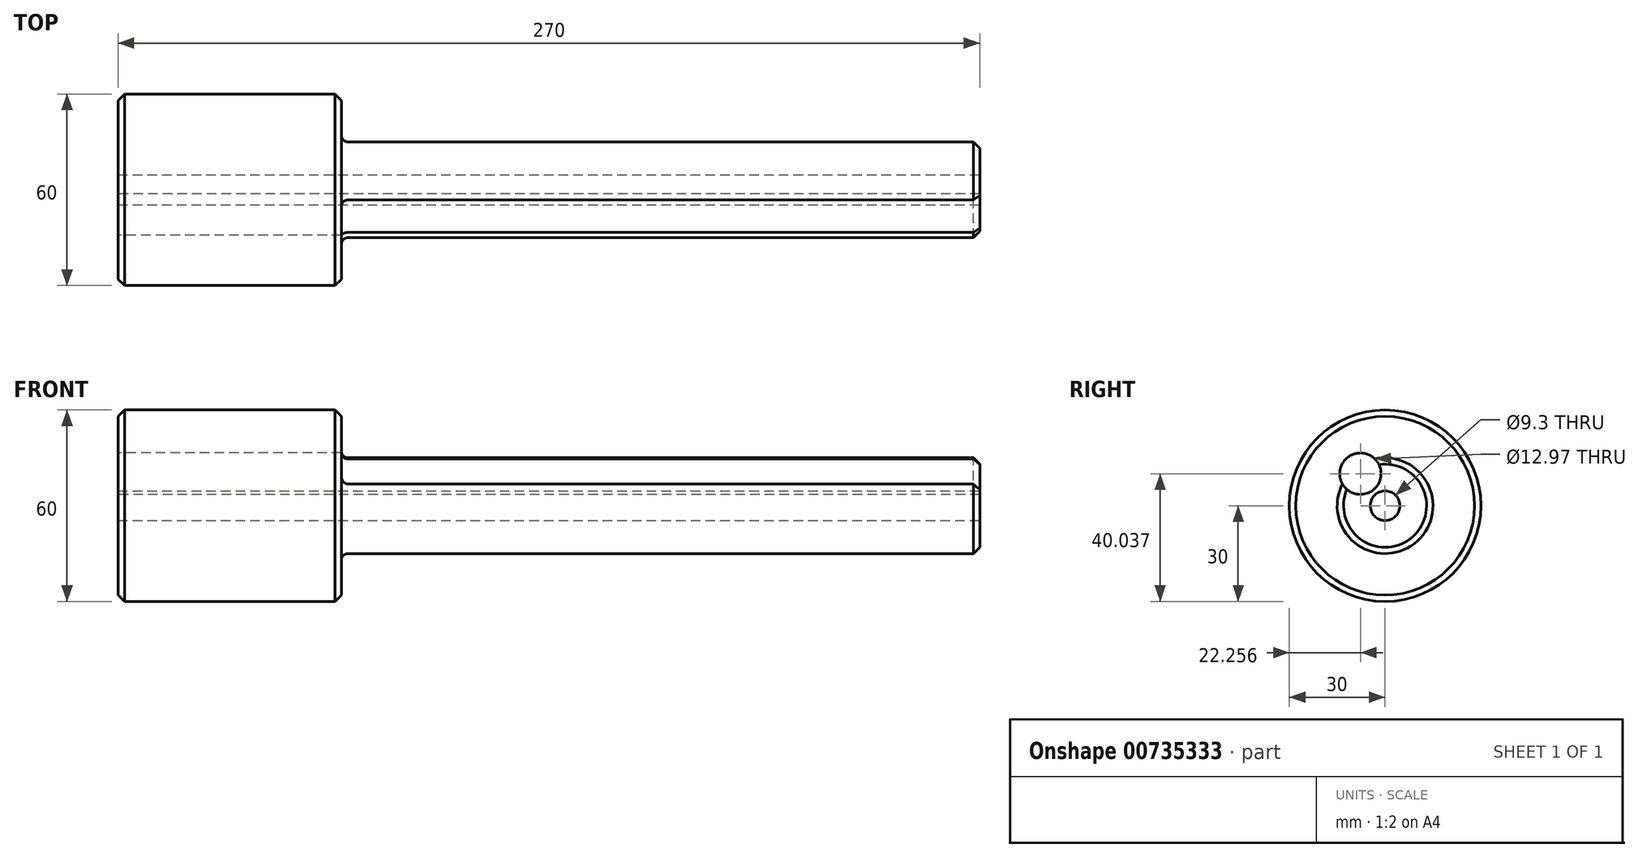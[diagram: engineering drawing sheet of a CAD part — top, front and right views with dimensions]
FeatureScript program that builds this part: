
annotation { "Feature Type Name" : "Feature", "Feature Type Description" : "" }
export const myFeature = defineFeature(function(context is Context, id is Id, definition is map)
    precondition{}
    {
        {
            var Q0;
            Q0=qCreatedBy(makeId("Front.planeOp"),FACE);
            var sketch = newSketch(context, id + "F0", { "sketchPlane" : qUnion([Q0])});
            skLineSegment(sketch, "E0", {"start": v(-135, 0) * mm, "end": v(-135, 30) * mm});
            skLineSegment(sketch, "E1", {"start": v(-135, 30) * mm, "end": v(-65, 30) * mm});
            skLineSegment(sketch, "E2", {"start": v(-65, 30) * mm, "end": v(-65, 17) * mm});
            skLineSegment(sketch, "E3", {"start": v(-63, 15) * mm, "end": v(135, 15) * mm});
            skLineSegment(sketch, "E4", {"start": v(135, 15) * mm, "end": v(135, 0) * mm});
            skLineSegment(sketch, "E5", {"start": v(135, 0) * mm, "end": v(-135, 0) * mm});
            skLineSegment(sketch, "E6", {"start": v(-172.19, 0) * mm, "end": v(191.82, 0) * mm, "construction": true});
            skPoint(sketch, "E7.visualSharp", {"position": v(-65, 15) * mm});
            skArc(sketch, "E7.filletArc", {"start": v(-65, 17) * mm, "mid": v(-64.41, 15.59) * mm, "end": v(-63, 15) * mm});
            skSolve(sketch);
        }
        {
            var Q0;
            Q0 = qSketchRegion(id + "F0", true);
            var Q1;
            Q1=sQuery(id+"F0.wireOp",EDGE,"E6");
            revolve(context, id + "F1", {"surfaceOperationType" : NewSurfaceOperationType.NEW, "entities" : qUnion([Q0]), "axis" : qUnion([Q1]), "revolveType" : RevolveType.FULL});
        }
        {
            var Q0;
            Q0=makeQuery(id+"F1.opRevolve","SWEPT_FACE",FACE,{"disambiguationData":[OSD([sQuery(id+"F0.wireOp",EDGE,"E1")])]});
            var Q1;
            Q1=makeQuery(id+"F1.opRevolve","SWEPT_EDGE",EDGE,{"disambiguationData":[OSD([sQuery(id+"F0.wireOp",EDGE,"E3"),sQuery(id+"F0.wireOp",EDGE,"E4")])]});
            chamfer(context, id + "F2", {"entities" : qUnion([Q0, Q1]), "chamferType" : ChamferType.OFFSET_ANGLE, "width" : 2 * mm, "oppositeDirection" : false, "angle" : 45 * degree, "tangentPropagation" : true});
        }
        {
            var Q0;
            Q0=makeQuery(id+"F1.opRevolve","SWEPT_FACE",FACE,{"disambiguationData":[OSD([sQuery(id+"F0.wireOp",EDGE,"E4")])]});
            var sketch = newSketch(context, id + "F3", { "sketchPlane" : qUnion([Q0])});
            skCircle(sketch, "E8", {"center": v(0, 0) * mm, "radius": 4.65 * mm});
            skSolve(sketch);
        }
        {
            var Q0;
            Q0 = qSketchRegion(id + "F3", true);
            extrude(context, id + "F4", {"entities" : qUnion([Q0]), "operationType" : NewBodyOperationType.REMOVE, "endBound" : BoundingType.THROUGH_ALL, "oppositeDirection" : true, "depth" : 25.4 * mm, "offsetDistance" : 25.4 * mm});
        }
        {
            var Q0;
            Q0=makeQuery(id+"F1.opRevolve","SWEPT_FACE",FACE,{"disambiguationData":[OSD([sQuery(id+"F0.wireOp",EDGE,"E0")])]});
            var sketch = newSketch(context, id + "F5", { "sketchPlane" : qUnion([Q0])});
            skCircle(sketch, "E9", {"center": v(7.74, 10.04) * mm, "radius": 6.48 * mm});
            skSolve(sketch);
        }
        {
            var Q0;
            Q0 = qSketchRegion(id + "F5", true);
            var sketch = newSketch(context, id + "F6", { "sketchPlane" : qUnion([Q0])});
            skSolve(sketch);
        }
        {
            var Q0;
            Q0=makeQuery(id+"F6.imprint","IMPRINT",FACE,{"disambiguationData":[TD([[makeQuery(id+"F6.imprint","IMPRINT",EDGE,{"derivedFrom":makeQuery(id+"F5.imprint","IMPRINT",EDGE,{"derivedFrom":sQuery(id+"F5.wireOp",EDGE,"E9")})}),1.0]])]});
            extrude(context, id + "F7", {"entities" : qUnion([Q0]), "operationType" : NewBodyOperationType.REMOVE, "endBound" : BoundingType.THROUGH_ALL, "oppositeDirection" : true, "depth" : 25.4 * mm, "offsetDistance" : 25.4 * mm});
        }
    });
